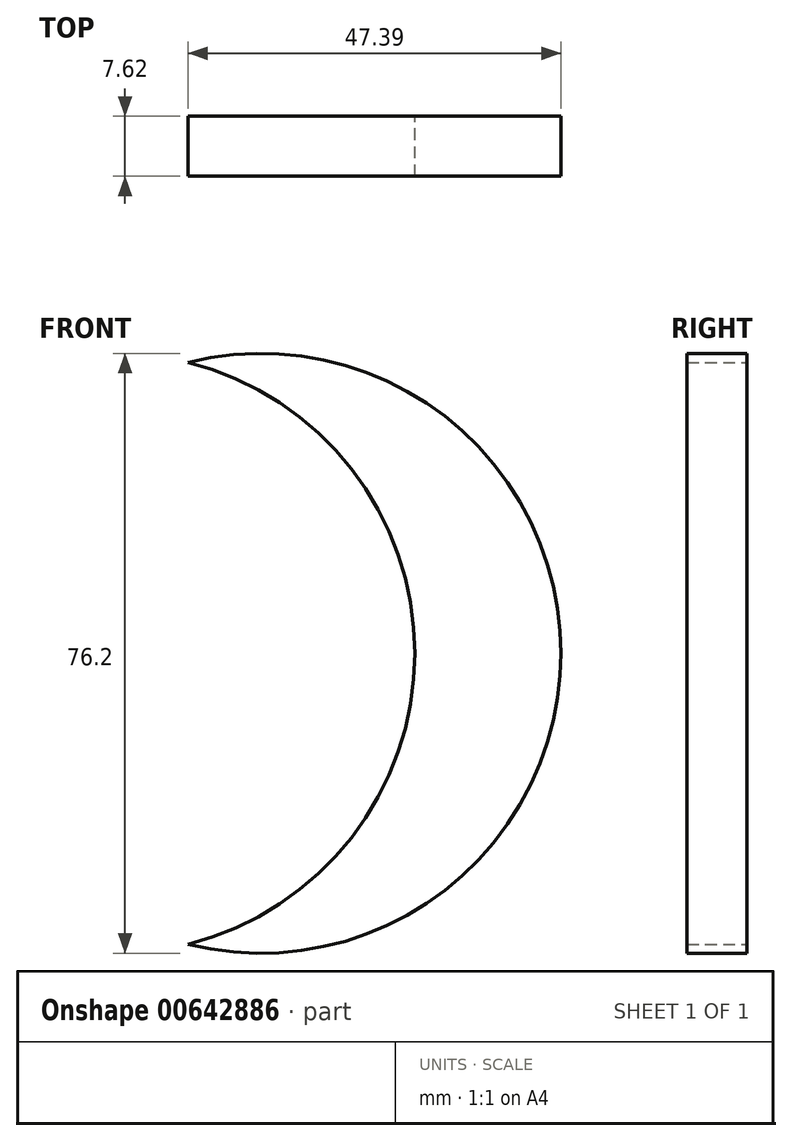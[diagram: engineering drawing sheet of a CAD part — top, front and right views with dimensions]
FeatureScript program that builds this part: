
annotation { "Feature Type Name" : "Feature", "Feature Type Description" : "" }
export const myFeature = defineFeature(function(context is Context, id is Id, definition is map)
    precondition{}
    {
        {
            var Q0;
            Q0=qCreatedBy(makeId("Front.planeOp"),FACE);
            var sketch = newSketch(context, id + "F0", { "sketchPlane" : qUnion([Q0])});
            skCircle(sketch, "E0", {"center": v(0, 0) * mm, "radius": 38.1 * mm});
            skCircle(sketch, "E1", {"center": v(-18.58, 0) * mm, "radius": 38.1 * mm});
            skSolve(sketch);
        }
        {
            var Q0;
            {var subQ0=sQuery(id+"F0.wireOp",EDGE,"E1");var subQ1=sQuery(id+"F0.wireOp",EDGE,"E0");var subQ2=makeQuery(id+"F0.imprint","INTERSECT",VERTEX,{"disambiguationData":[OD(0.0)],"derivedFrom":[subQ1,subQ0]});Q0=makeQuery(id+"F0.imprint","IMPRINT",FACE,{"disambiguationData":[TD([[makeQuery(id+"F0.imprint","IMPRINT",EDGE,{"disambiguationData":[TD([[subQ2,-1.0]])],"derivedFrom":subQ1}),1.0]])]});}
            extrude(context, id + "F1", {"entities" : qUnion([Q0]), "depth" : 7.62 * mm, "offsetDistance" : 25.4 * mm});
        }
    });
